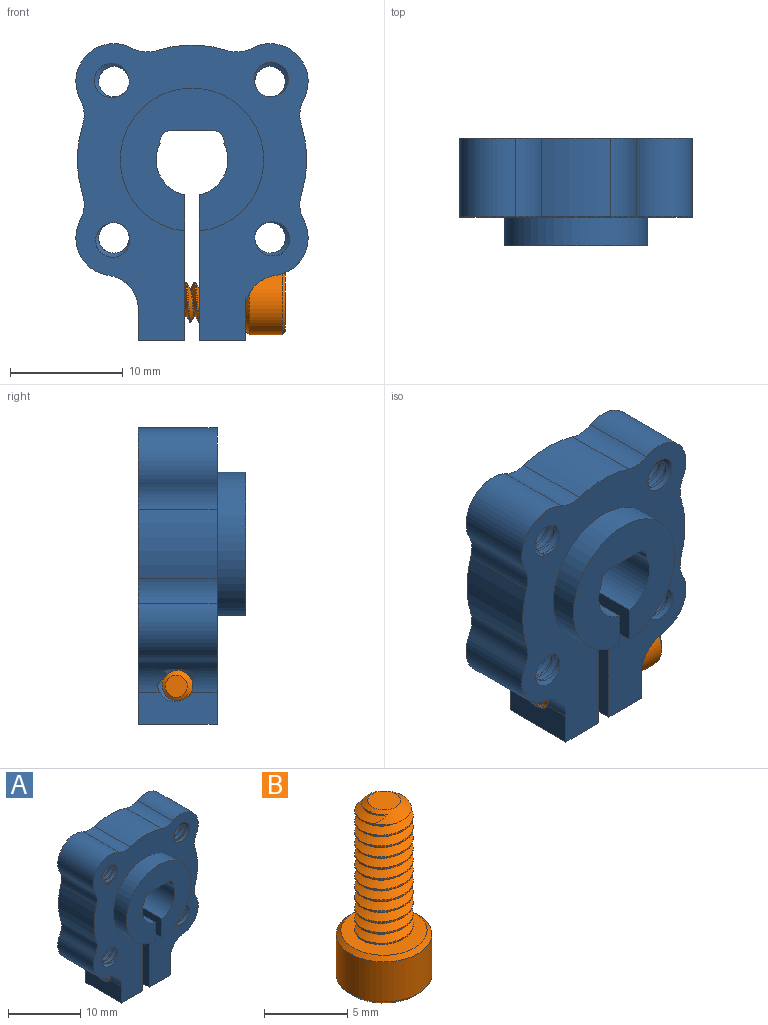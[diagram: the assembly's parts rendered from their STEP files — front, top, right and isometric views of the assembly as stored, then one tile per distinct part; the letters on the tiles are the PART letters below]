
ASSEMBLY  parts=2 mates=1
PART A: 56 faces, bbox 20.8x10.1x26.5 mm
  f0: cylinder r=1.75mm len=6.99mm, axis (0,-1,0), area 9.6mm2, adj f1,f53,f54,f55
  f1: plane 26.48x20.76mm, normal (0,1,0), area 379.8mm2, adj f0,f2,f3,f4,f5,f6,f7,f8
  f2: cylinder r=1.35mm len=6.99mm, axis (0,1,0), area 17.4mm2, adj f1,f53,f54,f55
  f3: bspline ~7.45x3.5mm, area 39.7mm2, adj f1,f4,f6,f54
  f4: cylinder r=1.35mm len=6.99mm, axis (0,1,0), area 17.4mm2, adj f1,f3,f5,f54
  f5: bspline ~7.71x3.93mm, area 39.8mm2, adj f1,f4,f6,f54
  f6: cylinder r=1.75mm len=6.99mm, axis (0,-1,0), area 9.6mm2, adj f1,f3,f5,f54
  f7: bspline ~7.45x3.5mm, area 39.7mm2, adj f1,f8,f10,f54
  f8: cylinder r=1.35mm len=6.99mm, axis (0,1,0), area 17.4mm2, adj f1,f7,f9,f54
  f9: bspline ~7.71x3.93mm, area 39.8mm2, adj f1,f8,f10,f54
  f10: cylinder r=1.75mm len=6.99mm, axis (0,-1,0), area 9.6mm2, adj f1,f7,f9,f54
  f11: bspline ~7.45x3.5mm, area 39.7mm2, adj f1,f12,f14,f54
  f12: cylinder r=1.35mm len=6.99mm, axis (0,1,0), area 17.4mm2, adj f1,f11,f13,f54
  f13: bspline ~7.71x3.93mm, area 39.8mm2, adj f1,f12,f14,f54
  f14: cylinder r=1.75mm len=6.99mm, axis (0,-1,0), area 9.6mm2, adj f1,f11,f13,f54
  f15: cylinder r=3.17mm len=9.53mm, axis (0,-1,0), area 55.6mm2, adj f1,f16,f18,f52
  f16: plane 12.7x12.67mm, normal (0,-1,0), area 91.9mm2, adj f15,f17,f18,f48,f49,f50,f51,f52
  f17: cylinder r=6.35mm len=12.7mm, axis (0,-1,0), area 98.1mm2, adj f16,f18,f48,f54
  f18: plane 12.89x9.53mm, normal (-1,0,0), area 88.3mm2, adj f1,f15,f16,f17,f19,f20,f54
  f19: cylinder r=1.78mm len=4.13mm, axis (1,0,0), area 46.1mm2, adj f18,f21
  f20: plane 6.99x4.13mm, normal (0,0,-1), area 28.8mm2, adj f1,f18,f21,f54
  f21: plane 6.99x6.92mm, normal (1,0,0), area 33.2mm2, adj f1,f19,f20,f22,f54
  f22: cylinder r=3.49mm len=6.99mm, axis (-1,0,0), area 29.3mm2, adj f1,f21,f23,f24,f25,f54
  f23: cylinder r=2.97mm len=2.52mm, axis (0,-1,0), area 1.6mm2, adj f22,f25,f54
  f24: cylinder r=2.97mm len=2.52mm, axis (0,-1,0), area 1.6mm2, adj f1,f22,f25
  f25: cylinder r=3.37mm len=6.99mm, axis (0,-1,0), area 35.3mm2, adj f1,f22,f23,f24,f26,f54
  f26: cylinder r=2.92mm len=6.99mm, axis (0,1,0), area 16.3mm2, adj f1,f25,f27,f54
  f27: cylinder r=10.16mm len=6.99mm, axis (0,-1,0), area 43.6mm2, adj f1,f26,f28,f54
  f28: cylinder r=2.92mm len=6.99mm, axis (0,1,0), area 16.3mm2, adj f1,f27,f29,f54
  f29: cylinder r=3.37mm len=6.99mm, axis (0,-1,0), area 60.1mm2, adj f1,f28,f30,f54
  f30: cylinder r=2.92mm len=6.99mm, axis (0,1,0), area 16.3mm2, adj f1,f29,f31,f54
  f31: cylinder r=10.16mm len=6.99mm, axis (0,-1,0), area 43.6mm2, adj f1,f30,f32,f54
  f32: cylinder r=2.92mm len=6.99mm, axis (0,1,0), area 16.3mm2, adj f1,f31,f33,f54
  f33: cylinder r=3.37mm len=6.99mm, axis (0,-1,0), area 60.1mm2, adj f1,f32,f34,f54
  f34: cylinder r=2.92mm len=6.99mm, axis (0,1,0), area 16.3mm2, adj f1,f33,f35,f54
  f35: cylinder r=10.16mm len=6.99mm, axis (0,-1,0), area 43.6mm2, adj f1,f34,f36,f54
  f36: cylinder r=2.92mm len=6.99mm, axis (0,1,0), area 16.3mm2, adj f1,f35,f37,f54
  f37: cylinder r=3.37mm len=6.99mm, axis (0,-1,0), area 45.5mm2, adj f1,f36,f38,f54
  f38: cylinder r=2.97mm len=6.99mm, axis (0,-1,0), area 23.9mm2, adj f1,f37,f39,f40,f41,f42,f43,f44
  f39: bspline ~4.66x3.96mm, area 23.5mm2, adj f38,f40,f42,f46,f48
  f40: cylinder r=1.75mm len=4.21mm, axis (-1,0,0), area 5.8mm2, adj f38,f39,f41,f48
  f41: bspline ~4.93x3.96mm, area 24.5mm2, adj f38,f40,f42,f48
  f42: cylinder r=1.35mm len=4.59mm, axis (1,0,0), area 11.1mm2, adj f38,f39,f41,f43,f46,f48
  f43: bspline ~2.9x1.31mm, area 1.4mm2, adj f38,f42,f45
  f44: bspline ~3.64x2.34mm, area 0mm2, adj f38,f45
  f45: cylinder r=1.75mm len=2.68mm, axis (-1,0,0), area 0.3mm2, adj f38,f43,f44
  f46: plane 7.09x2.91mm, normal (-1,0,0), area 18mm2, adj f1,f38,f39,f42,f47,f54
  f47: plane 6.99x4.13mm, normal (0,0,-1), area 28.8mm2, adj f1,f46,f48,f54
  f48: plane 13.08x9.71mm, normal (1,0,0), area 90.9mm2, adj f1,f16,f17,f39,f40,f41,f42,f47
  f49: cylinder r=3.17mm len=9.53mm, axis (0,-1,0), area 55.6mm2, adj f1,f16,f48,f50
  f50: cylinder r=1mm len=9.53mm, axis (0,-1,0), area 16.4mm2, adj f1,f16,f49,f51
  f51: plane 9.53x3.69mm, normal (0,0,-1), area 35.1mm2, adj f1,f16,f50,f52
  f52: cylinder r=1mm len=9.53mm, axis (0,-1,0), area 16.4mm2, adj f1,f15,f16,f51
  f53: bspline ~7.45x3.5mm, area 39.7mm2, adj f0,f1,f2,f54
  f54: plane 26.48x20.76mm, normal (0,-1,0), area 287.9mm2, adj f0,f2,f3,f4,f5,f6,f7,f8
  f55: bspline ~7.71x3.93mm, area 39.8mm2, adj f0,f1,f2,f54
PART B: 24 faces, bbox 6.3x6.3x13.8 mm
  f0: cone r=2.87mm half-angle=45deg, axis (0,0,-1), area 7mm2, adj f1,f8
  f1: plane 5.47x5.47mm, normal (0,0,1), area 13.8mm2, adj f0,f2,f5,f6,f7
  f2: bspline ~9.94x3.46mm, area 64.7mm2, adj f1,f3,f5,f7
  f3: cone r=0.98mm half-angle=55deg, axis (0,0,-1), area 5mm2, adj f2,f4,f5,f6,f7
  f4: plane 1.97x1.97mm, normal (0,0,1), area 3mm2, adj f3
  f5: cylinder r=1.24mm len=9.35mm, axis (0,0,-1), area 9.1mm2, adj f1,f2,f3,f6
  f6: bspline ~9.65x3.5mm, area 64.7mm2, adj f1,f3,f5,f7
  f7: cylinder r=1.75mm len=8.99mm, axis (0,0,1), area 12.4mm2, adj f1,f2,f3,f6
  f8: cylinder r=2.87mm len=5.74mm, axis (0,0,1), area 52.9mm2, adj f0,f9
  f9: cone r=2.58mm half-angle=45deg, axis (0,0,1), area 7mm2, adj f8,f10
  f10: plane 5.17x5.17mm, normal (0,0,-1), area 12.9mm2, adj f9,f11,f19,f20,f21,f22,f23
  f11: cone r=1.6mm half-angle=45deg, axis (0,0,-1), area 0mm2, adj f10,f12
  f12: plane 2.69x2mm, normal (-0.5,-0.87,0), area 3.1mm2, adj f11,f13,f17,f18
  f13: plane 3.21x2.78mm, normal (0,0,-1), area 6.7mm2, adj f12,f14,f15,f16,f17,f18
  f14: plane 2.24x1.76mm, normal (1,0,0), area 3.1mm2, adj f13,f15,f18,f22
  f15: plane 2.69x2mm, normal (0.5,0.87,0), area 3.1mm2, adj f13,f14,f16,f21
  f16: plane 2.69x2mm, normal (-0.5,0.87,0), area 3.1mm2, adj f13,f15,f17,f20
  f17: plane 2.69x2.21mm, normal (-1,0,0), area 3.1mm2, adj f12,f13,f16,f19
  f18: plane 2.69x2mm, normal (0.5,-0.87,0), area 3.1mm2, adj f12,f13,f14,f23
  f19: cone r=1.6mm half-angle=45deg, axis (0,0,-1), area 0mm2, adj f10,f17
  f20: cone r=1.6mm half-angle=45deg, axis (0,0,-1), area 0mm2, adj f10,f16
  f21: cone r=1.6mm half-angle=45deg, axis (0,0,-1), area 0mm2, adj f10,f15
  f22: cone r=1.6mm half-angle=45deg, axis (0,0,-1), area 0.2mm2, adj f10,f14
  f23: cone r=1.6mm half-angle=45deg, axis (0,0,-1), area 0mm2, adj f10,f18
PLACE A t=(-23.64,11.02,14.78)mm
PLACE B rot(axis=(0,-1,0),90deg) t=(-28.4,17.17,2.16)mm
MATE fastened A.f22 <-> B.f1  axis (1,0,0) through (-18.87,17.05,2.21)mm
